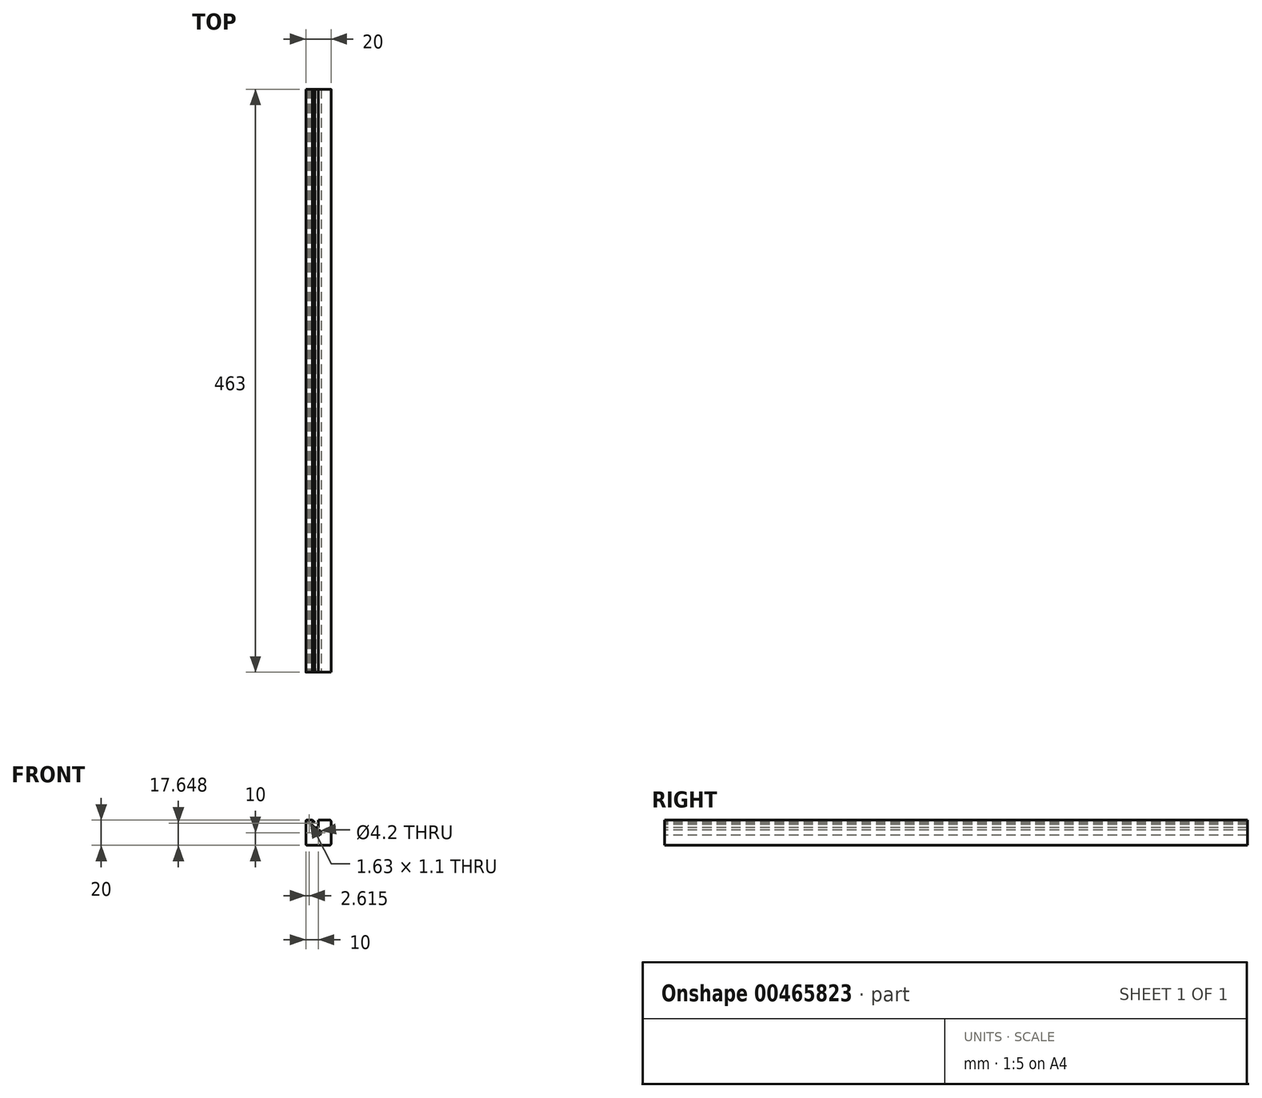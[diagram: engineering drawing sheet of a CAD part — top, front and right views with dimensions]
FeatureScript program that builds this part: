
annotation { "Feature Type Name" : "Feature", "Feature Type Description" : "" }
export const myFeature = defineFeature(function(context is Context, id is Id, definition is map)
    precondition{}
    {
        {
            var Q0;
            Q0=qCreatedBy(makeId("Front.planeOp"),FACE);
            var sketch = newSketch(context, id + "F0", { "sketchPlane" : qUnion([Q0])});
            skLineSegment(sketch, "E0.bottom", {"start": v(10, 10) * mm, "end": v(-10, 10) * mm});
            skLineSegment(sketch, "E0.top", {"start": v(10, -10) * mm, "end": v(-10, -10) * mm});
            skLineSegment(sketch, "E0.left", {"start": v(10, 10) * mm, "end": v(10, -10) * mm});
            skLineSegment(sketch, "E0.right", {"start": v(-10, 10) * mm, "end": v(-10, -10) * mm});
            skPoint(sketch, "E0.middle", {"position": v(0, 0) * mm});
            skSolve(sketch);
        }
        {
            var Q0;
            Q0 = qSketchRegion(id + "F0", true);
            extrude(context, id + "F1", {"entities" : qUnion([Q0]), "depth" : 463 * mm});
        }
        {
            var Q0;
            Q0=makeQuery(id+"F1.opExtrude","CAP_FACE",FACE,{"disambiguationData":[OSD([sQuery(id+"F0.wireOp",EDGE,"E0.bottom"),sQuery(id+"F0.wireOp",EDGE,"E0.top"),sQuery(id+"F0.wireOp",EDGE,"E0.left"),sQuery(id+"F0.wireOp",EDGE,"E0.right")])],"isStart":false});
            var sketch = newSketch(context, id + "F2", { "sketchPlane" : qUnion([Q0])});
            skCircle(sketch, "E1", {"center": v(0, 0) * mm, "radius": 2.1 * mm});
            skSolve(sketch);
        }
        {
            var Q0;
            Q0 = qSketchRegion(id + "F2", true);
            extrude(context, id + "F3", {"entities" : qUnion([Q0]), "operationType" : NewBodyOperationType.REMOVE, "endBound" : BoundingType.THROUGH_ALL, "oppositeDirection" : true, "depth" : 25 * mm});
        }
        {
            var Q0;
            Q0=makeQuery(id+"F1.opExtrude","SWEPT_EDGE",EDGE,{"disambiguationData":[OSD([sQuery(id+"F0.wireOp",EDGE,"E0.bottom"),sQuery(id+"F0.wireOp",EDGE,"E0.right")])]});
            var Q1;
            Q1=makeQuery(id+"F1.opExtrude","SWEPT_EDGE",EDGE,{"disambiguationData":[OSD([sQuery(id+"F0.wireOp",EDGE,"E0.bottom"),sQuery(id+"F0.wireOp",EDGE,"E0.left")])]});
            var Q2;
            Q2=makeQuery(id+"F1.opExtrude","SWEPT_EDGE",EDGE,{"disambiguationData":[OSD([sQuery(id+"F0.wireOp",EDGE,"E0.top"),sQuery(id+"F0.wireOp",EDGE,"E0.left")])]});
            var Q3;
            Q3=makeQuery(id+"F1.opExtrude","SWEPT_EDGE",EDGE,{"disambiguationData":[OSD([sQuery(id+"F0.wireOp",EDGE,"E0.top"),sQuery(id+"F0.wireOp",EDGE,"E0.right")])]});
            fillet(context, id + "F4", {"entities" : qUnion([Q0, Q1, Q2, Q3]), "radius" : 1 * mm, "tangentPropagation" : true, "allowEdgeOverflow" : false});
        }
        {
            var Q0;
            Q0=makeQuery(id+"F1.opExtrude","CAP_FACE",FACE,{"disambiguationData":[OSD([sQuery(id+"F0.wireOp",EDGE,"E0.bottom"),sQuery(id+"F0.wireOp",EDGE,"E0.top"),sQuery(id+"F0.wireOp",EDGE,"E0.left"),sQuery(id+"F0.wireOp",EDGE,"E0.right")])],"isStart":false});
            var sketch = newSketch(context, id + "F5", { "sketchPlane" : qUnion([Q0])});
            skLineSegment(sketch, "E2", {"start": v(0, 10) * mm, "end": v(-2.84, 10) * mm});
            skLineSegment(sketch, "E3", {"start": v(-2.84, 10) * mm, "end": v(-2.84, 8.2) * mm, "construction": true});
            skLineSegment(sketch, "E4", {"start": v(-2.84, 8.2) * mm, "end": v(-5.5, 8.2) * mm});
            skLineSegment(sketch, "E5", {"start": v(-2.84, 3.9) * mm, "end": v(0, 3.9) * mm});
            skLineSegment(sketch, "E6", {"start": v(0, 3.9) * mm, "end": v(0, 10) * mm});
            skLineSegment(sketch, "E7", {"start": v(-5.5, 8.2) * mm, "end": v(-5.5, 6.56) * mm});
            skLineSegment(sketch, "E8", {"start": v(-5.5, 6.56) * mm, "end": v(-2.84, 3.9) * mm});
            skPoint(sketch, "E9.endSnap0", {"position": v(-1.42, 3.9) * mm});
            skLineSegment(sketch, "E10", {"start": v(0, 0) * mm, "end": v(-9.7, 9.7) * mm, "construction": true});
            skLineSegment(sketch, "E11", {"start": v(-2.84, 8.2) * mm, "end": v(-4.64, 10) * mm});
            skLineSegment(sketch, "E12", {"start": v(-4.64, 10) * mm, "end": v(-2.84, 10) * mm});
            skLineSegment(sketch, "E13", {"start": v(-8.2, 8.2) * mm, "end": v(-6.57, 8.2) * mm});
            skLineSegment(sketch, "E14", {"start": v(-6.57, 8.2) * mm, "end": v(-6.57, 7.62) * mm});
            skLineSegment(sketch, "E15", {"start": v(-6.57, 7.62) * mm, "end": v(-7.1, 7.1) * mm});
            skLineSegment(sketch, "E16", {"start": v(-7.1, 7.1) * mm, "end": v(-8.2, 8.2) * mm});
            skSolve(sketch);
        }
        {
            var Q0;
            Q0 = qSketchRegion(id + "F5", true);
            extrude(context, id + "F6", {"entities" : qUnion([Q0]), "operationType" : NewBodyOperationType.REMOVE, "endBound" : BoundingType.THROUGH_ALL, "oppositeDirection" : true, "depth" : 25 * mm});
        }
        {
            var Q0;
            Q0=qCreatedBy(makeId("Top.planeOp"),FACE);
            var sketch = newSketch(context, id + "F7", { "sketchPlane" : qUnion([Q0])});
            skLineSegment(sketch, "E17", {"start": v(0, 0) * mm, "end": v(0, -25.58) * mm, "construction": true});
            skSolve(sketch);
        }
    });
